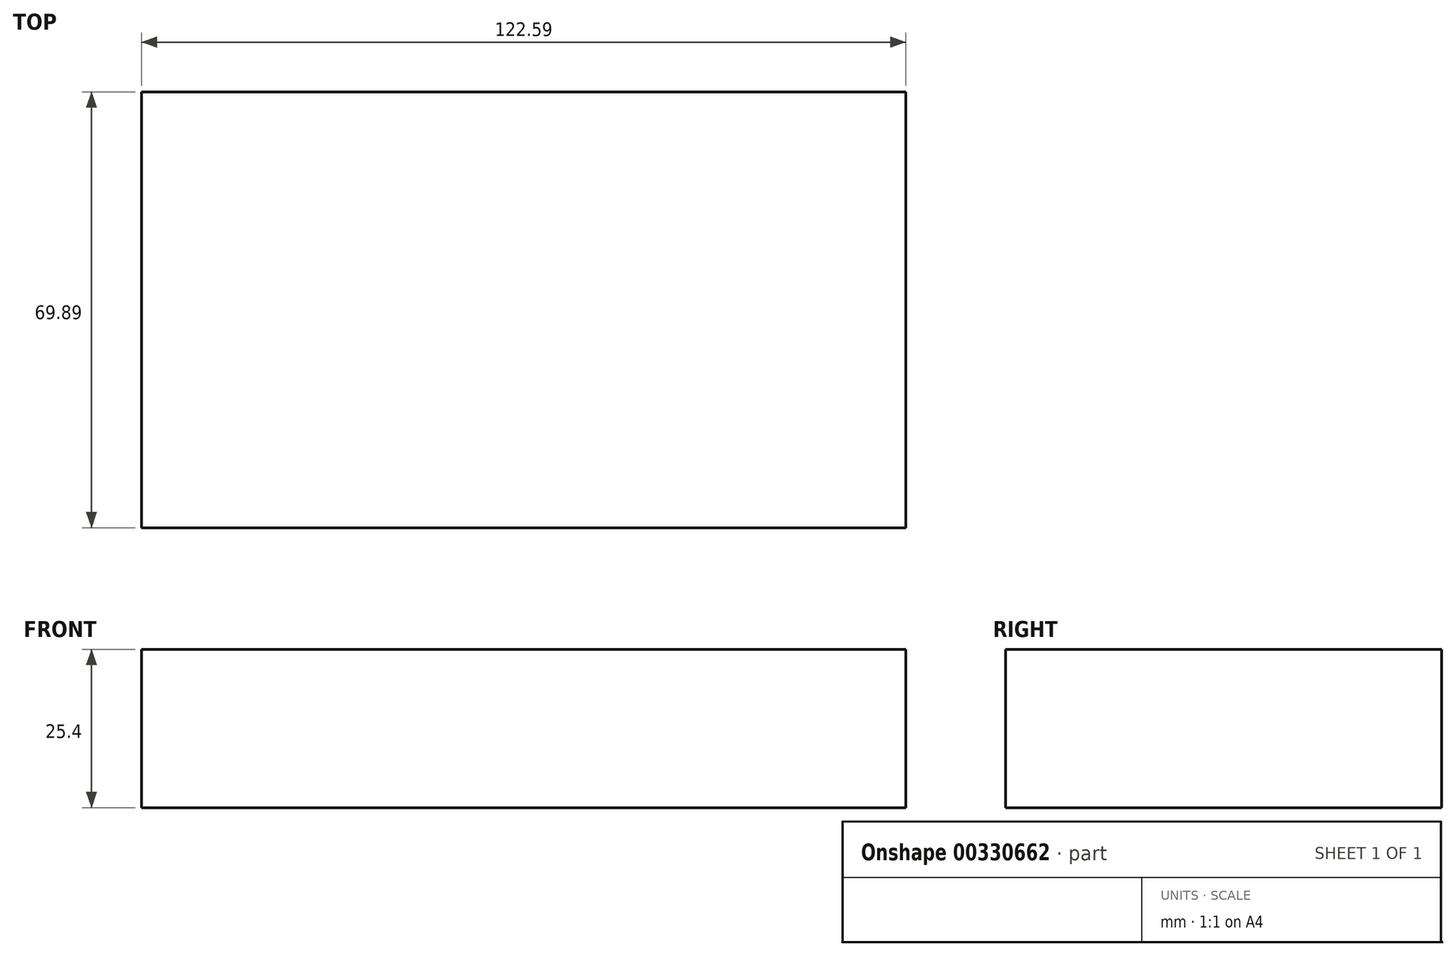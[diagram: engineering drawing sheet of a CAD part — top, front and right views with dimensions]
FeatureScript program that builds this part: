
annotation { "Feature Type Name" : "Feature", "Feature Type Description" : "" }
export const myFeature = defineFeature(function(context is Context, id is Id, definition is map)
    precondition{}
    {
        {
            var Q0;
            Q0=qCreatedBy(makeId("Top.planeOp"),FACE);
            var sketch = newSketch(context, id + "F0", { "sketchPlane" : qUnion([Q0])});
            skLineSegment(sketch, "E0.bottom", {"start": v(-98.31, 46.58) * mm, "end": v(24.28, 46.58) * mm});
            skLineSegment(sketch, "E0.top", {"start": v(-98.31, -23.31) * mm, "end": v(24.28, -23.31) * mm});
            skLineSegment(sketch, "E0.left", {"start": v(-98.31, 46.58) * mm, "end": v(-98.31, -23.31) * mm});
            skLineSegment(sketch, "E0.right", {"start": v(24.28, 46.58) * mm, "end": v(24.28, -23.31) * mm});
            skSolve(sketch);
        }
        {
            var Q0;
            Q0 = qSketchRegion(id + "F0", true);
            extrude(context, id + "F1", {"entities" : qUnion([Q0]), "depth" : 25.4 * mm});
        }
    });
